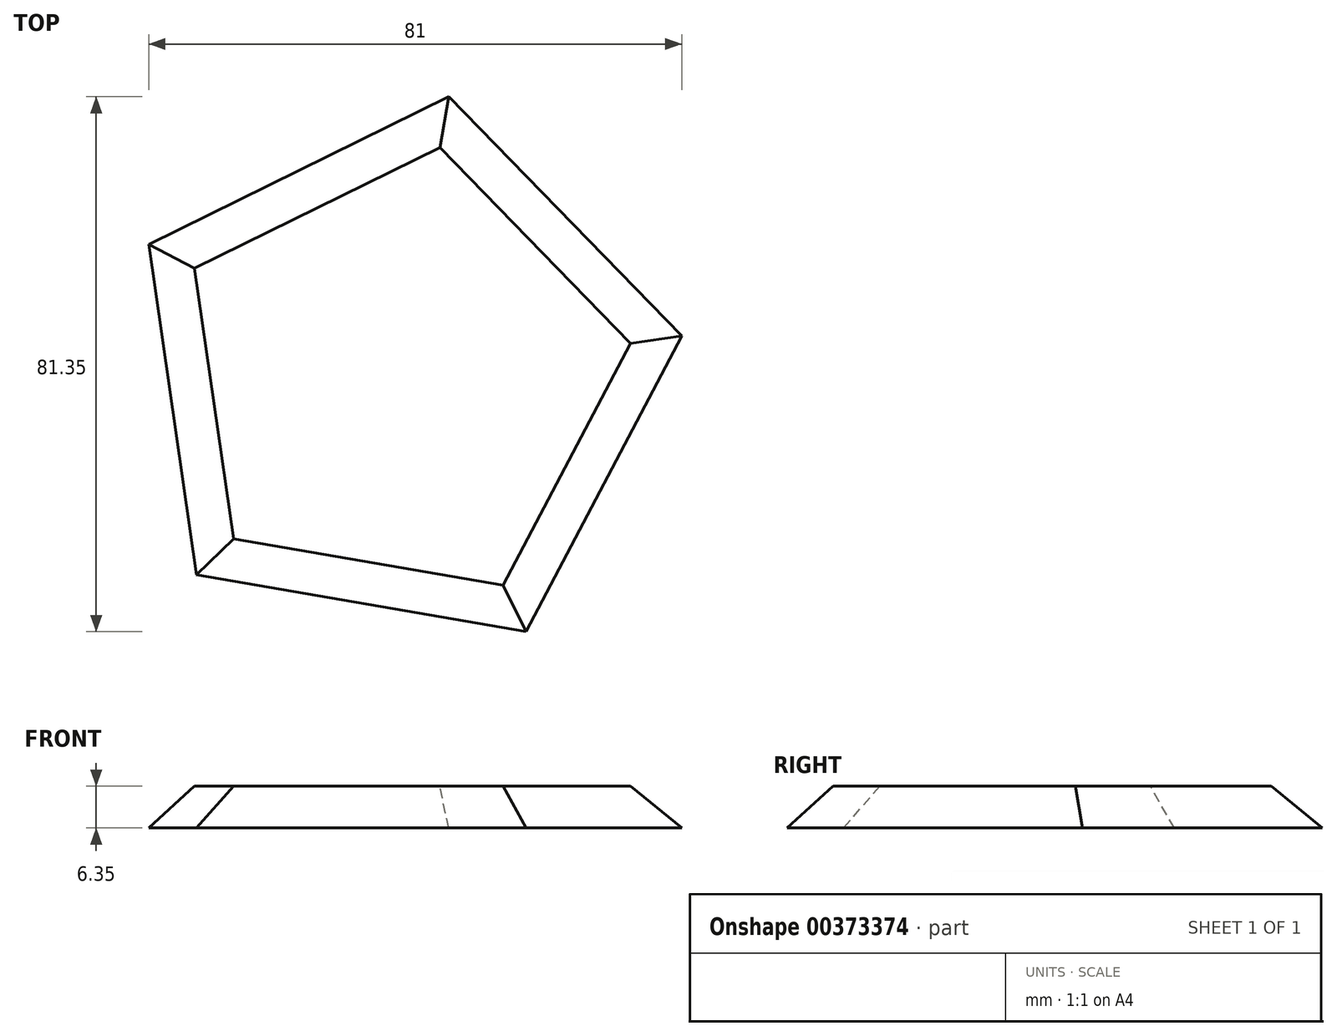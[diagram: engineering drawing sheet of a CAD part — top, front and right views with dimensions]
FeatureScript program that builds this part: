
annotation { "Feature Type Name" : "Feature", "Feature Type Description" : "" }
export const myFeature = defineFeature(function(context is Context, id is Id, definition is map)
    precondition{}
    {
        {
            var Q0;
            Q0=qCreatedBy(makeId("Top.planeOp"),FACE);
            var sketch = newSketch(context, id + "F0", { "sketchPlane" : qUnion([Q0])});
            skCircle(sketch, "E0.cCircle", {"center": v(0, 0) * mm, "radius": 34.96 * mm, "construction": true});
            skLineSegment(sketch, "E0.0", {"start": v(-38.23, 20.14) * mm, "end": v(7.34, 42.58) * mm});
            skLineSegment(sketch, "E0.1", {"start": v(7.34, 42.58) * mm, "end": v(42.77, 6.18) * mm});
            skLineSegment(sketch, "E0.2", {"start": v(42.77, 6.18) * mm, "end": v(19.1, -38.77) * mm});
            skLineSegment(sketch, "E0.3", {"start": v(19.1, -38.77) * mm, "end": v(-30.97, -30.14) * mm});
            skLineSegment(sketch, "E0.4", {"start": v(-30.97, -30.14) * mm, "end": v(-38.23, 20.14) * mm});
            skPoint(sketch, "E0.0.midPoint", {"position": v(-15.45, 31.36) * mm});
            skSolve(sketch);
        }
        {
            var Q0;
            Q0=makeQuery(id+"F0.imprint","IMPRINT",FACE,{"disambiguationData":[TD([[makeQuery(id+"F0.imprint","IMPRINT",EDGE,{"derivedFrom":sQuery(id+"F0.wireOp",EDGE,"E0.0")}),-1.0]])]});
            extrude(context, id + "F1", {"entities" : qUnion([Q0]), "depth" : 6.35 * mm});
        }
        {
            var Q0;
            Q0=makeQuery(id+"F1.opExtrude","CAP_EDGE",EDGE,{"disambiguationData":[OSD([sQuery(id+"F0.wireOp",EDGE,"E0.2")])],"isStart":false});
            var Q1;
            Q1=makeQuery(id+"F1.opExtrude","CAP_EDGE",EDGE,{"disambiguationData":[OSD([sQuery(id+"F0.wireOp",EDGE,"E0.1")])],"isStart":false});
            var Q2;
            Q2=makeQuery(id+"F1.opExtrude","CAP_EDGE",EDGE,{"disambiguationData":[OSD([sQuery(id+"F0.wireOp",EDGE,"E0.0")])],"isStart":false});
            var Q3;
            Q3=makeQuery(id+"F1.opExtrude","CAP_EDGE",EDGE,{"disambiguationData":[OSD([sQuery(id+"F0.wireOp",EDGE,"E0.3")])],"isStart":false});
            var Q4;
            Q4=makeQuery(id+"F1.opExtrude","CAP_FACE",FACE,{"disambiguationData":[OSD([sQuery(id+"F0.wireOp",EDGE,"E0.0"),sQuery(id+"F0.wireOp",EDGE,"E0.1"),sQuery(id+"F0.wireOp",EDGE,"E0.2"),sQuery(id+"F0.wireOp",EDGE,"E0.3"),sQuery(id+"F0.wireOp",EDGE,"E0.4")])],"isStart":false});
            chamfer(context, id + "F2", {"entities" : qUnion([Q0, Q1, Q2, Q3, Q4]), "width" : 6.35 * mm, "tangentPropagation" : true});
        }
    });
